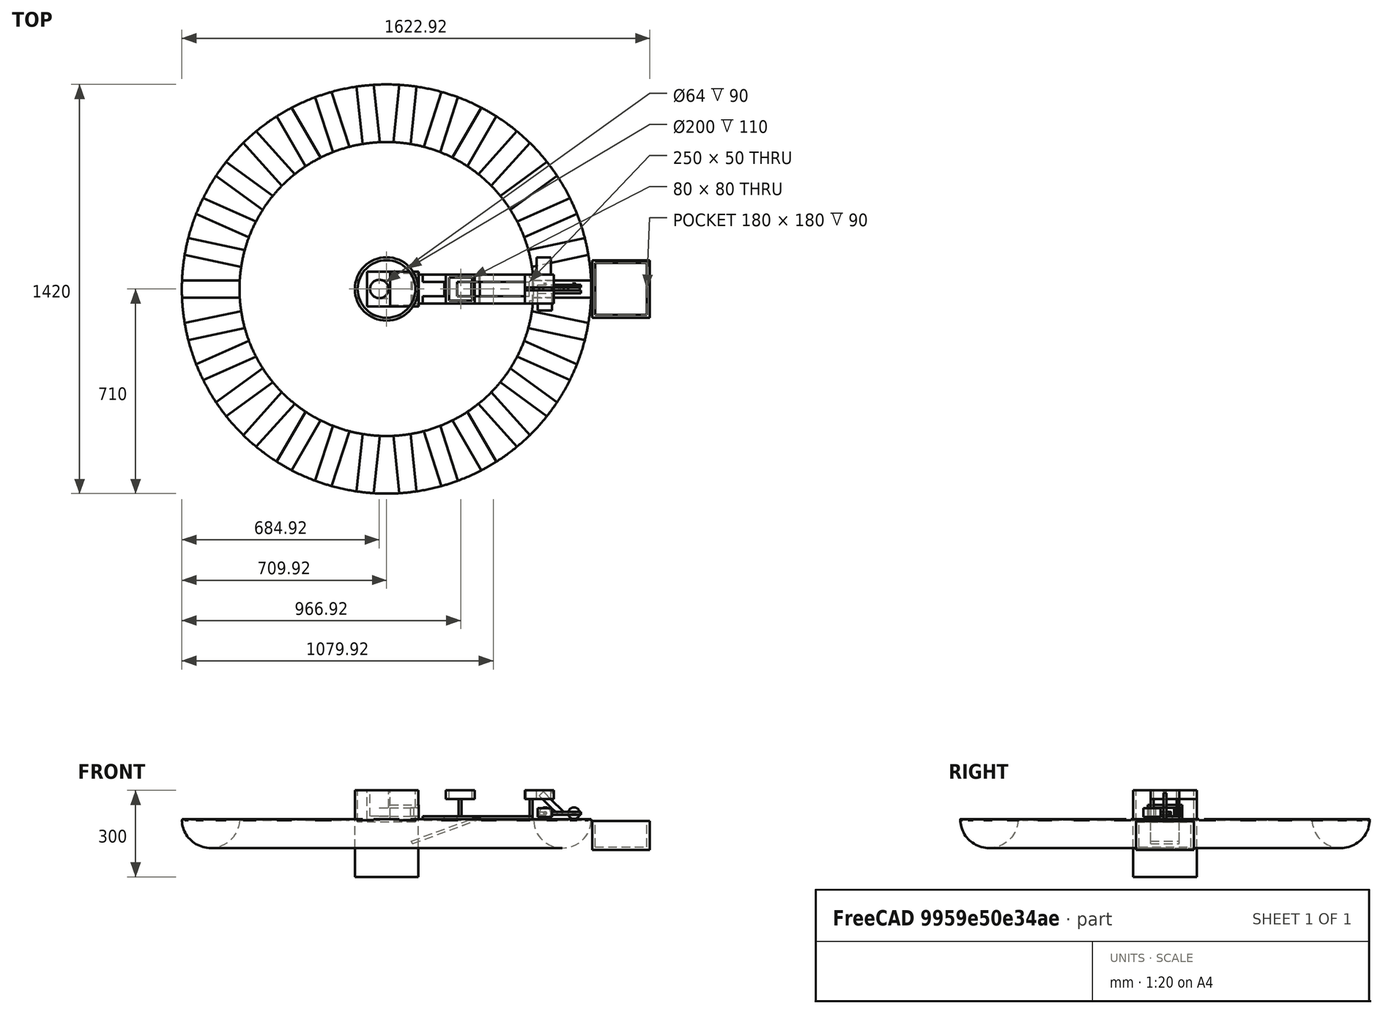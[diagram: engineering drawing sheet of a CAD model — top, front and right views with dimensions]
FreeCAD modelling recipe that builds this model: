
FCSTD DOCUMENT  (FreeCAD 0.15R4671 (Git))
Label: Kartensortiermaschine_CAD
License: All rights reserved
LicenseURL: http://en.wikipedia.org/wiki/All_rights_reserved
objects: Part::Box×31, Part::Cut×19, Part::Cylinder×7, Part::Torus×3, Part::FeaturePython×1
note: 61 computed .brp shape members not serialized (recipe doc carries the construction recipe); baked Part::Feature solids carry a one-line shape summary decoded from their .brp

FEATURE [Part::Torus] Torus
  Angle1 = -180
  Angle2 = 180
  Angle3 = 360
  Radius1 = 610
  Radius2 = 100
FEATURE [Part::Box] Box  label="Würfel"
  Height = 150
  Length = 1500
  Placement = pos=(-750,-750,0) rot=(0,0,1;0rad)
  Width = 1500
FEATURE [Part::Cut] Cut
  Base = -> Torus
  Tool = -> Box
FEATURE [Part::Cylinder] Cylinder  label="Zylinder"
  Angle = 360
  Height = 300
  Placement = pos=(0,0,-200) rot=(0,0,1;0rad)
  Radius = 110
FEATURE [Part::Box] Box001  label="Würfel001"
  Height = 50
  Length = 100
  Placement = pos=(12,-60,0) rot=(0,0,1;0rad)
  Width = 120
FEATURE [Part::Box] Box003  label="Würfel003"
  Height = 30
  Length = 120
  Placement = pos=(4,-55,10) rot=(0,0,1;0rad)
  Width = 110
FEATURE [Part::Box] Box004  label="Würfel004"
  Height = 30
  Length = 120
  Placement = pos=(4,-55,10) rot=(0,0,1;0rad)
  Width = 110
FEATURE [Part::Cut] Cut003
  Base = -> Box001
  Tool = -> Box004
FEATURE [Part::Box] Box007  label="Würfel005"
  Height = 10
  Length = 380
  Placement = pos=(126,-50,0) rot=(0,0,1;0rad)
  Width = 100
FEATURE [Part::Cylinder] Cylinder001  label="Zylinder001"
  Angle = 360
  Height = 300
  Placement = pos=(0,0,-10) rot=(0,0,1;0rad)
  Radius = 100
FEATURE [Part::Cut] Cut004
  Base = -> Cylinder
  Tool = -> Cylinder001
FEATURE [Part::Box] Box008  label="Würfel006"
  Height = 30
  Length = 120
  Placement = pos=(4,-55,10) rot=(0,0,1;0rad)
  Width = 110
FEATURE [Part::Cut] Cut005
  Base = -> Cut004
  Tool = -> Box008
FEATURE [Part::Cut] Cut006
  Base = -> Cut003
  Tool = -> Box003
FEATURE [Part::Box] Box009  label="Würfel007"
  Height = 10
  Length = 100
  Placement = pos=(100,-25,0) rot=(0,0,1;0rad)
  Width = 50
FEATURE [Part::Box] Box010  label="Würfel008"
  Height = 10
  Length = 100
  Placement = pos=(100,-25,0) rot=(0,0,1;0rad)
  Width = 50
FEATURE [Part::Cut] Cut007
  Base = -> Box007
  Tool = -> Box010
FEATURE [Part::Cut] Cut008
  Base = -> Cut006
  Tool = -> Box009
FEATURE [Part::Box] Box011  label="Würfel009"
  Height = 10
  Length = 250
  Placement = pos=(245,-25,0) rot=(0,0,1;0rad)
  Width = 50
FEATURE [Part::Cut] Cut009
  Base = -> Cut007
  Tool = -> Box011
FEATURE [Part::Box] Box012  label="Würfel010"
  Height = 10
  Length = 250
  Placement = pos=(90,-50,-85) rot=(0,-1,0;0.349066rad)
  Width = 100
FEATURE [Part::Box] Box013  label="Würfel011"
  Height = 10
  Length = 100
  Placement = pos=(260,-25,0) rot=(0,0,1;0rad)
  Width = 50
FEATURE [Part::Cut] Cut010
  Base = -> Box012
  Tool = -> Box013
FEATURE [Part::Box] Box014  label="Würfel012"
  Height = 100
  Length = 80
  Placement = pos=(-68,-60,0) rot=(0,0,1;0rad)
  Width = 120
FEATURE [Part::Cylinder] Cylinder002  label="Zylinder002"
  Angle = 360
  Height = 90
  Placement = pos=(-25,0,10) rot=(0,0,1;0rad)
  Radius = 32
FEATURE [Part::Cut] Cut011
  Base = -> Box014
  Tool = -> Cylinder002
FEATURE [Part::Box] Box015  label="Würfel013"
  Height = 30
  Length = 50
  Placement = pos=(-25,-32,10) rot=(0,0,1;0rad)
  Width = 64
FEATURE [Part::Cut] Cut012
  Base = -> Cut011
  Tool = -> Box015
FEATURE [Part::Cylinder] Cylinder003  label="Zylinder003"
  Angle = 360
  Height = 10
  Placement = pos=(550,5,21) rot=(1,0,0;1.5708rad)
  Radius = 20
FEATURE [Part::Cylinder] Cylinder004  label="Zylinder004"
  Angle = 360
  Height = 10
  Placement = pos=(650,5,21) rot=(1,0,0;1.5708rad)
  Radius = 20
FEATURE [Part::Box] Box016  label="Würfel014"
  Height = 10
  Length = 150
  Placement = pos=(524,-15,15) rot=(0,0,1;0rad)
  Width = 10
FEATURE [Part::Box] Box017  label="Würfel015"
  Height = 10
  Length = 150
  Placement = pos=(524,5,15) rot=(0,0,1;0rad)
  Width = 10
FEATURE [Part::Box] Box018  label="Würfel016"
  Height = 100
  Length = 20
  Placement = pos=(600,-5,11) rot=(0,-1,0;0.785398rad)
  Width = 10
FEATURE [Part::Box] Box019  label="Würfel017"
  Height = 10
  Length = 150
  Placement = pos=(524,-5,5) rot=(0,0,1;0rad)
  Width = 10
FEATURE [Part::Cut] Cut013
  Base = -> Box018
  Tool = -> Box019
FEATURE [Part::Cylinder] Cylinder005  label="Zylinder005"
  Angle = 360
  Height = 5
  Placement = pos=(550,20,21) rot=(1,0,0;1.5708rad)
  Radius = 5
FEATURE [Part::Torus] Torus001
  Angle1 = -180
  Angle2 = 180
  Angle3 = 360
  Placement = pos=(550,17.5,21) rot=(0.999938,0,0.01111;1.5708rad)
  Radius1 = 5
  Radius2 = 2
FEATURE [Part::Cut] Cut014
  Base = -> Cylinder005
  Tool = -> Torus001
FEATURE [Part::Cylinder] Cylinder006  label="Zylinder006"
  Angle = 360
  Height = 5
  Placement = pos=(550,20,21) rot=(1,0,0;1.5708rad)
  Radius = 5
FEATURE [Part::Torus] Torus002
  Angle1 = -180
  Angle2 = 180
  Angle3 = 360
  Placement = pos=(550,17.5,21) rot=(0.999938,0,0.01111;1.5708rad)
  Radius1 = 5
  Radius2 = 2
FEATURE [Part::Cut] Cut015
  Base = -> Cylinder006
  Placement = pos=(100,0,0) rot=(0,0,1;0rad)
  Tool = -> Torus002
FEATURE [Part::Box] Box020  label="Würfel018"
  Height = 30
  Length = 50
  Placement = pos=(524,-75,8) rot=(0,0,1;0rad)
  Width = 60
FEATURE [Part::Box] Box021  label="Würfel019"
  Height = 10
  Length = 60
  Placement = pos=(496,40,70) rot=(0,1,0;1.5708rad)
  Width = 10
FEATURE [Part::Box] Box022  label="Würfel020"
  Height = 10
  Length = 60
  Placement = pos=(496,-50,70) rot=(0,1,0;1.5708rad)
  Width = 10
FEATURE [Part::Box] Box023  label="Würfel021"
  Height = 30
  Length = 100
  Placement = pos=(480,-50,70) rot=(0,0,1;0rad)
  Width = 100
FEATURE [Part::Box] Box024  label="Würfel022"
  Height = 30
  Length = 90
  Placement = pos=(485,-5,70) rot=(0,0,1;0rad)
  Width = 10
FEATURE [Part::Box] Box025  label="Würfel023"
  Height = 30
  Length = 90
  Placement = pos=(570,-5,60) rot=(0,0,1;0rad)
  Width = 10
FEATURE [Part::Cut] Cut016
  Base = -> Box023
  Tool = -> Box024
FEATURE [Part::Cut] Cut017
  Base = -> Cut016
  Tool = -> Box025
FEATURE [Part::Box] Box026  label="Würfel024"
  Height = 30
  Length = 50
  Placement = pos=(520,50,70) rot=(0,0,1;0rad)
  Width = 60
FEATURE [Part::Box] Box027  label="Würfel025"
  Height = 10
  Length = 60
  Placement = pos=(250,-50,70) rot=(0,1,0;1.5708rad)
  Width = 10
FEATURE [Part::Box] Box028  label="Würfel026"
  Height = 10
  Length = 60
  Placement = pos=(250,40,70) rot=(0,1,0;1.5708rad)
  Width = 10
FEATURE [Part::Box] Box029  label="Würfel027"
  Height = 30
  Length = 100
  Placement = pos=(206,-50,70) rot=(0,0,1;0rad)
  Width = 100
FEATURE [Part::Box] Box030  label="Würfel028"
  Height = 30
  Length = 80
  Placement = pos=(217,-40,70) rot=(0,0,1;0rad)
  Width = 80
FEATURE [Part::Cut] Cut018
  Base = -> Box029
  Tool = -> Box030
FEATURE [Part::Box] Box034  label="Würfel032"
  Height = 100
  Length = 200
  Placement = pos=(715,-100,-100) rot=(0,0,1;0rad)
  Width = 200
FEATURE [Part::Box] Box035  label="Würfel033"
  Height = 90
  Length = 180
  Placement = pos=(725,-90,-90) rot=(0,0,1;0rad)
  Width = 180
FEATURE [Part::Cut] Cut019
  Base = -> Box034
  Placement = pos=(-2,0,-6) rot=(0,0,1;0rad)
  Tool = -> Box035
FEATURE [Part::Box] Box036  label="Karte1"
  Height = 30
  Length = 206
  Placement = pos=(507,-30,-4) rot=(0,0,1;0rad)
  Width = 60
FEATURE [Part::FeaturePython] Array  # Draft array (typed FeaturePython)
  Angle = 360
  ArrayType = 1
  Axis = (0,0,1)
  Base = -> Box036
  Center = (0,0,0)
  Fuse = false
  IntervalAxis = (0,0,0)
  IntervalX = (0,65,0)
  IntervalY = (0,1,0)
  IntervalZ = (0,0,0)
  NumberPolar = 30
  NumberX = 55
  NumberY = 0
  NumberZ = 0
FEATURE [Part::Cut] Cut020
  Base = -> Cut
  Tool = -> Array
